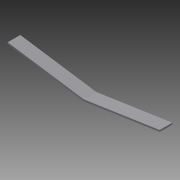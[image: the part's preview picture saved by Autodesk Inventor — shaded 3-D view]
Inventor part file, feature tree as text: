
AUTODESK INVENTOR PART (.ipt)
format: ipt  version: 2013 (Build 170138000, 138)  size: 72,192 bytes
history: native  units: in
note: dims shown in document units (in); Inventor stores cm internally (conversion verified against a paired STEP export)
features: extrude x1, sketch x1
ambient origin geometry x8: Origin, YZ Plane, XZ Plane, XY Plane, X Axis, Y Axis, Z Axis, Center Point
bodies: Solid1 (feature_tree)
feature tree (2):
  extrude  "Extrusion1"  Depth=12.0in
  sketch  "Sketch1"  dims[d0=0.9in d2=12.0in d3=90.0deg d4=0.125in d5=0.125in d6=1.0in d7=0.0in]
